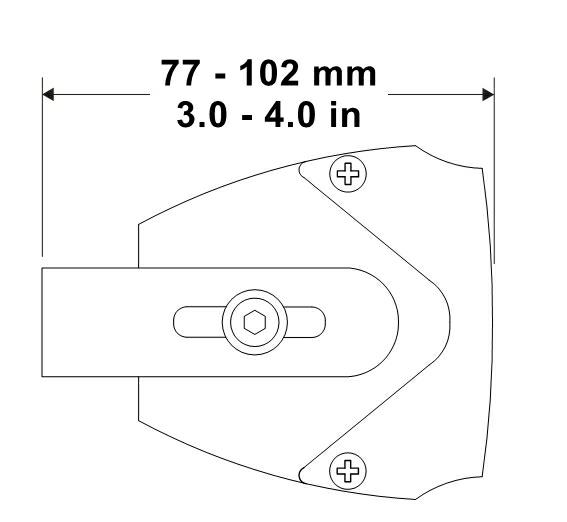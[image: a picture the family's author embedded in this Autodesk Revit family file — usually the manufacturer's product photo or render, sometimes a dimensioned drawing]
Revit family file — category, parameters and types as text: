
# Revit family: Electronics_Desono_Biamp_Two-Way-Column-Loudspeaker_COLW101
name_source: partatom
category: Communication Devices
units: mm (PartAtom-declared; Revit-internal decimal feet)

## family parameters
Cut with Voids When Loaded = No
Host = Face
Maintain Annotation Orientation = No
OmniClass Number = 23.85.10.11.14.14.14
OmniClass Title = Loudspeakers
Part Type = Normal
Room Calculation Point = No
Round Connector Dimension = Use Diameter
Shared = No

## types (1)
- COLW101
    Bracket Material = Biamp - Metal - White
    Connector Description = Terminal block; Low impedance 8 ohms, 70V/100V operation
    Continuous Power Handling Nominal Impedance = 28V; 100W @ 8Ω (400W peak)
    Controls = None; select transformer tap or low impedance input via terminal block wiring
    Default Elevation = 4' - 0"
    Depth = 0' - 3 1/2"
    Description = Desono™ COLW101 Two-Way 10 x 3.3 Column Loudspeaker
    Environmental = IP66 per IEC 60529
    Grill Material = Biamp - Plastic - White(Grid)
    Height = 3' - 10 1/2"
    Housing Material = Biamp - Plastic - White
    Input Connection = Multi-position pass-through, screw-down terminal block
    Manufacturer = Biamp
    Model = COLW101
    Mounting Provisions = Adjustable tilt L-bracket
    Nominal Beamwidth (H x V) = 100° x 8°
    Nominal Maximum SPL @ 1m = Peak - 125dB; Continuous - 119dB
    Nominal Sensitivity @ 1m = 1W - 99dB; 2.83V - 99dB
    Operating Environment = Indoor/Outdoor
    Operating Mode = Passive
    Operating Range (-10dB) = 165 Hz to 18 kHz
    Product Documentation Link = https://downloads.biamp.com
    Product Page URL = https://www.biamp.com
    Product data url = https://www.bimobject.com
    Recommended Amplifers = 100W - 200W @ 8Ω (28V - 40V)
    Shipping Weight = 19.18 lb
    Transducers = LF 10 x 3.3 (84 mm) coated paper cone HF 1 x 1 (25 mm) soft dome
    Transformer = 70V: 100W, 50W, 30W, 20W; 100V: 100W, 60W, 40W
    URL = https://www.biamp.com
    Weight = 16.98 lb
    Width = 0' - 4"

## geometry (parser evidence)
native form markers: Sweep x5
no freeform markers — native parametric forms only
